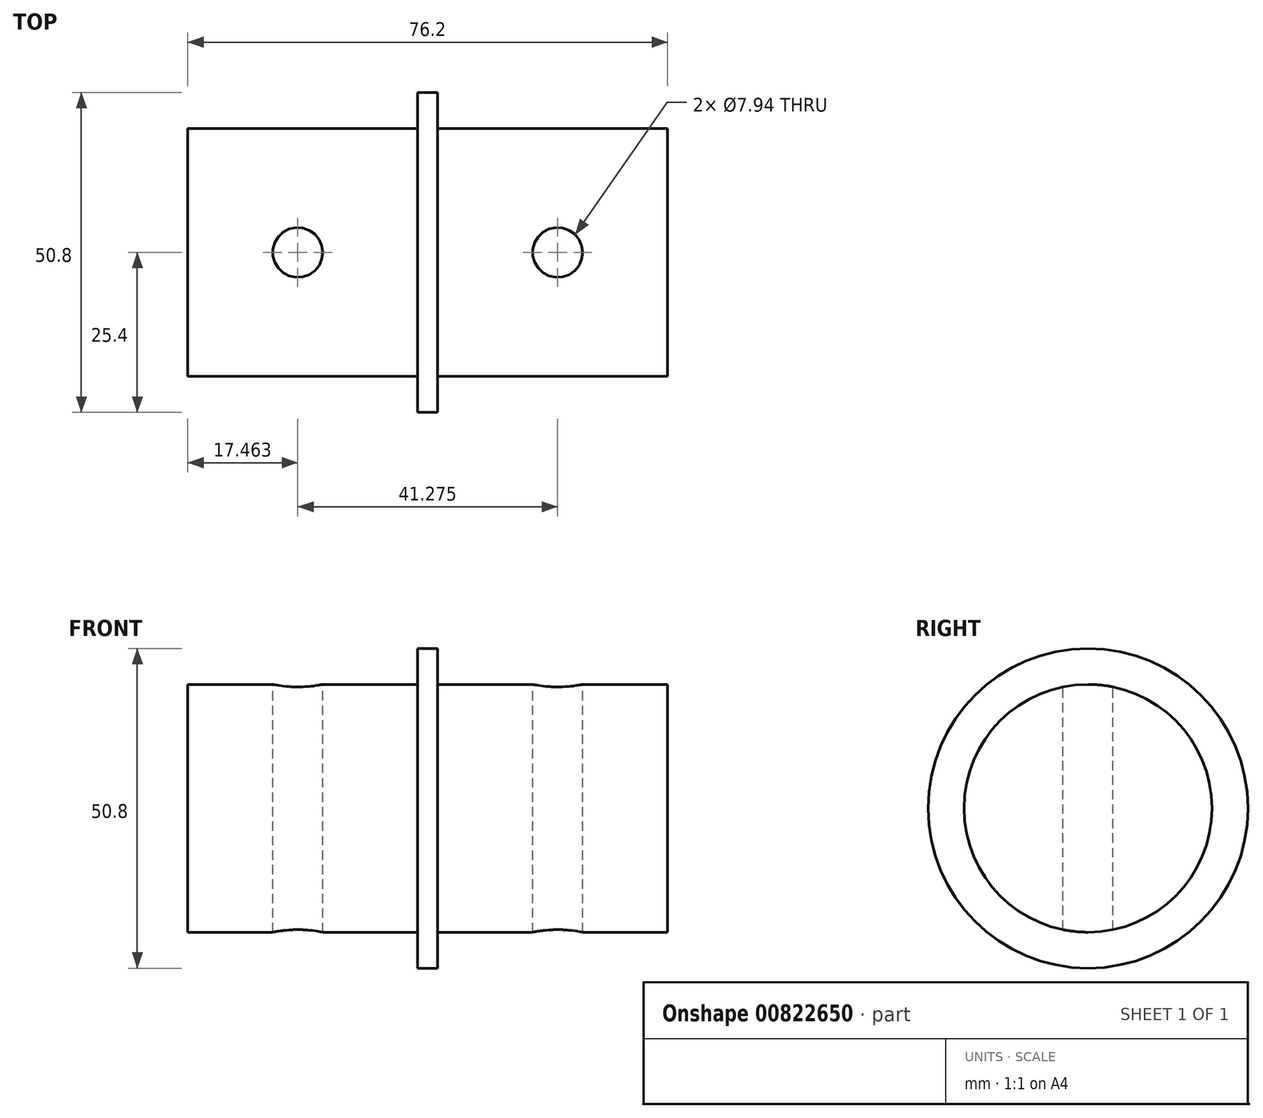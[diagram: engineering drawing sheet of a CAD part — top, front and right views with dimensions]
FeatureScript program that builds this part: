
annotation { "Feature Type Name" : "Feature", "Feature Type Description" : "" }
export const myFeature = defineFeature(function(context is Context, id is Id, definition is map)
    precondition{}
    {
        {
            var Q0;
            Q0=qCreatedBy(makeId("Right.planeOp"),FACE);
            var sketch = newSketch(context, id + "F0", { "sketchPlane" : qUnion([Q0])});
            skCircle(sketch, "E0", {"center": v(0, 0) * mm, "radius": 19.69 * mm});
            skSolve(sketch);
        }
        {
            var Q0;
            Q0 = qSketchRegion(id + "F0", true);
            extrude(context, id + "F1", {"entities" : qUnion([Q0]), "endBound" : BoundingType.SYMMETRIC, "depth" : 76.2 * mm, "offsetDistance" : 25.4 * mm});
        }
        {
            var Q0;
            Q0=qCreatedBy(makeId("Right.planeOp"),FACE);
            var sketch = newSketch(context, id + "F2", { "sketchPlane" : qUnion([Q0])});
            skCircle(sketch, "E1", {"center": v(0, 0) * mm, "radius": 25.4 * mm});
            skSolve(sketch);
        }
        {
            var Q0;
            Q0 = qSketchRegion(id + "F2", true);
            extrude(context, id + "F3", {"entities" : qUnion([Q0]), "operationType" : NewBodyOperationType.ADD, "endBound" : BoundingType.SYMMETRIC, "depth" : 3.17 * mm, "offsetDistance" : 25.4 * mm});
        }
        {
            var Q0;
            Q0=qCreatedBy(makeId("Top.planeOp"),FACE);
            cPlane(context, id + "F4", {"entities" : qUnion([Q0]), "cplaneType" : CPlaneType.OFFSET, "offset" : 25.4 * mm, "width" : 152.4 * mm, "height" : 152.4 * mm});
        }
        {
            var Q0;
            Q0=qCreatedBy(id+"F4.planeOp",FACE);
            var sketch = newSketch(context, id + "F5", { "sketchPlane" : qUnion([Q0])});
            skPoint(sketch, "E2", {"position": v(-20.64, 0) * mm});
            skPoint(sketch, "E3", {"position": v(20.64, 0) * mm});
            skSolve(sketch);
        }
        {
            var Q0;
            Q0=sQuery(id+"F5.wireOp",VERTEX,"E2");
            var Q1;
            Q1=sQuery(id+"F5.wireOp",VERTEX,"E3");
            var Q2;
            Q2=makeQuery(id+"F1.opExtrude","SWEPT_BODY",BODY,{"disambiguationData":[OSD([sQuery(id+"F0.wireOp",EDGE,"E0")])]});
            hole(context, id + "F6", {"style" : HoleStyle.SIMPLE, "endStyle" : HoleEndStyle.THROUGH, "standardTappedOrClearance" : lookupTablePath({ "standard" : "ANSI", "engagement" : "75%", "pitch" : "16 tpi", "size" : "3/8", "type" : "Tapped" }), "standardBlindInLast" : lookupTablePath({ "standard" : "ANSI", "engagement" : "75%", "pitch" : "16 tpi", "size" : "3/8", "type" : "Tapped" }), "holeDiameter" : 7.94 * mm, "majorDiameter" : 9.52 * mm, "showTappedDepth" : true, "isTappedThrough" : true, "tappedDepth" : 12.7 * mm, "tapClearance" : 3, "locations" : qUnion([Q0, Q1]), "scope" : qUnion([Q2])});
        }
    });
